# Revit family: 3-543-xx - 37-543-xx - Orion (Vanity)
name_source: partatom
category: Luminarias
revit_build: Autodesk Revit 2018 (Build: 20170223_1515(x64)
units: mm (PartAtom-declared; Revit-internal decimal feet)

## family parameters
Anfitrión = Cara
Compartido = No
Corte con vacíos al cargar = No
Cota de conector redondo = Diámetro de uso
Origen de luz = Sí
Punto de cálculo de habitación = No
Tipo de pieza = Normal

## types (8) — shared parameters
Anchura rectángulo de emisión = 22 "
Archivo de red fotométrica = 3-543 Orion Vanity.ies
Cambio de temperatura de color de luz atenuada = <Ninguno>
Comentarios de vataje = 13.8 W at 120 V
Fabricante = Oxygen - Lighting & Fans
Filtro de color = 16777215
Forma visible en renderización = No
Longitud de rectángulo de emisión = 1 "
Lámpara = LED Array
Main Diffuser = Matte White Acrylic
Modelo = 3-543-XX / 37-543-XX - Orion Vanity
URL = www.oxygenlighting.com
Ángulo de inclinación = 180.00°
zero-valued in all types: Elevación por defecto

## per-type parameters (varying)
| type | Metal Finish | Voltage |
| 3-543-15 / Black - Matte White Acrylic | 15 - Black | 120 V |
| 3-543-20 / Polished Nickel - Matte White Acrylic | 20 - Polished Nickel | 120 V |
| 3-543-24 / Satin Nickel - Matte White Acrylic | 24 - Satin Nickel | 120 V |
| 3-543-14 / Polished Chrome - Matte White Acrylic | 14 - Polished Chrome | 120 V |
| 37-543-14 / Polished Chrome - Matte White Acrylic | 14 - Polished Chrome | 277 V |
| 37-543-15 / Black - Matte White Acrylic | 15 - Black | 277 V |
| 37-543-20 / Polished Nickel - Matte White Acrylic | 20 - Polished Nickel | 277 V |
| 37-543-24 / Satin Nickel - Matte White Acrylic | 24 - Satin Nickel | 277 V |

## geometry (parser evidence)
native form markers: Extrusion x1, Sweep x13
no freeform markers — native parametric forms only
